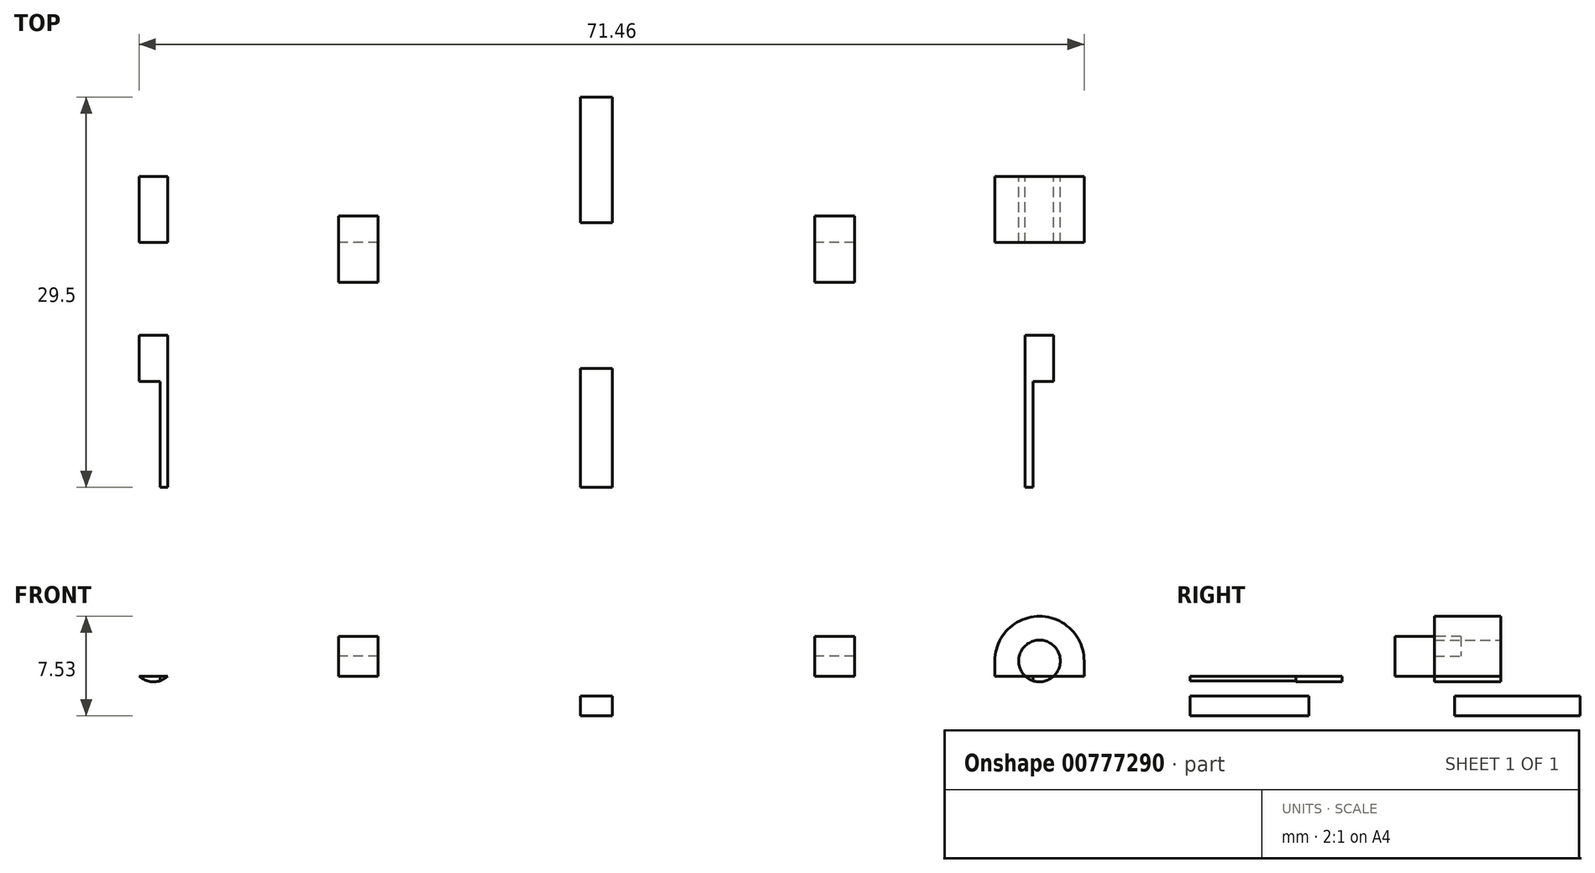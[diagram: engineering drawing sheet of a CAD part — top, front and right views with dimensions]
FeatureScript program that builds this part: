
annotation { "Feature Type Name" : "Feature", "Feature Type Description" : "" }
export const myFeature = defineFeature(function(context is Context, id is Id, definition is map)
    precondition{}
    {
        {
            var Q0;
            Q0=qCreatedBy(makeId("Top.planeOp"),FACE);
            var sketch = newSketch(context, id + "F0", { "sketchPlane" : qUnion([Q0])});
            skLineSegment(sketch, "E0.bottom", {"start": v(-40, 11.75) * mm, "end": v(40, 11.75) * mm});
            skLineSegment(sketch, "E0.top", {"start": v(-40, -11.75) * mm, "end": v(40, -11.75) * mm});
            skLineSegment(sketch, "E0.left", {"start": v(-40, 11.75) * mm, "end": v(-40, -11.75) * mm});
            skLineSegment(sketch, "E0.right", {"start": v(40, 11.75) * mm, "end": v(40, -11.75) * mm});
            skLineSegment(sketch, "E1", {"start": v(-83.31, 0) * mm, "end": v(90.72, 0) * mm, "construction": true});
            skLineSegment(sketch, "E2", {"start": v(0, 73.48) * mm, "end": v(0, -78.32) * mm, "construction": true});
            skLineSegment(sketch, "E3.bottom", {"start": v(-40, -11.75) * mm, "end": v(-33, -11.75) * mm});
            skLineSegment(sketch, "E3.top", {"start": v(-40, -3.75) * mm, "end": v(-33, -3.75) * mm});
            skLineSegment(sketch, "E3.left", {"start": v(-40, -11.75) * mm, "end": v(-40, -3.75) * mm});
            skLineSegment(sketch, "E3.right", {"start": v(-33, -11.75) * mm, "end": v(-33, -3.75) * mm});
            skLineSegment(sketch, "E4.bottom", {"start": v(40, -11.75) * mm, "end": v(33, -11.75) * mm});
            skLineSegment(sketch, "E4.top", {"start": v(40, -3.75) * mm, "end": v(33, -3.75) * mm});
            skLineSegment(sketch, "E4.left", {"start": v(40, -11.75) * mm, "end": v(40, -3.75) * mm});
            skLineSegment(sketch, "E4.right", {"start": v(33, -11.75) * mm, "end": v(33, -3.75) * mm});
            skLineSegment(sketch, "E5.bottom", {"start": v(-3, 8.25) * mm, "end": v(3, 8.25) * mm});
            skLineSegment(sketch, "E5.top", {"start": v(-3, -2.75) * mm, "end": v(3, -2.75) * mm});
            skLineSegment(sketch, "E5.left", {"start": v(-3, 8.25) * mm, "end": v(-3, -2.75) * mm});
            skLineSegment(sketch, "E5.right", {"start": v(3, 8.25) * mm, "end": v(3, -2.75) * mm});
            skLineSegment(sketch, "E6.bottom", {"start": v(-19.5, 8.75) * mm, "end": v(-16.5, 8.75) * mm});
            skLineSegment(sketch, "E6.top", {"start": v(-19.5, 3.75) * mm, "end": v(-16.5, 3.75) * mm});
            skLineSegment(sketch, "E6.left", {"start": v(-19.5, 8.75) * mm, "end": v(-19.5, 3.75) * mm});
            skLineSegment(sketch, "E6.right", {"start": v(-16.5, 8.75) * mm, "end": v(-16.5, 3.75) * mm});
            skLineSegment(sketch, "E7.bottom", {"start": v(16.5, 8.75) * mm, "end": v(19.5, 8.75) * mm});
            skLineSegment(sketch, "E7.top", {"start": v(16.5, 3.75) * mm, "end": v(19.5, 3.75) * mm});
            skLineSegment(sketch, "E7.left", {"start": v(16.5, 8.75) * mm, "end": v(16.5, 3.75) * mm});
            skLineSegment(sketch, "E7.right", {"start": v(19.5, 8.75) * mm, "end": v(19.5, 3.75) * mm});
            skLineSegment(sketch, "E8.bottom", {"start": v(37, -0.25) * mm, "end": v(30, -0.25) * mm});
            skLineSegment(sketch, "E8.top", {"start": v(37, 6.75) * mm, "end": v(30, 6.75) * mm});
            skLineSegment(sketch, "E8.left", {"start": v(37, -0.25) * mm, "end": v(37, 6.75) * mm});
            skLineSegment(sketch, "E8.right", {"start": v(30, -0.25) * mm, "end": v(30, 6.75) * mm});
            skLineSegment(sketch, "E9.MirrorCS", {"start": v(-30, -0.25) * mm, "end": v(-30, 6.75) * mm});
            skLineSegment(sketch, "E10.MirrorCS", {"start": v(-37, -0.25) * mm, "end": v(-37, 6.75) * mm});
            skLineSegment(sketch, "E11.MirrorCS", {"start": v(-37, -0.25) * mm, "end": v(-30, -0.25) * mm});
            skLineSegment(sketch, "E12.MirrorCS", {"start": v(-37, 6.75) * mm, "end": v(-30, 6.75) * mm});
            skSolve(sketch);
        }
        {
            var Q0;
            Q0=makeQuery(id+"F0.imprint","IMPRINT",FACE,{"disambiguationData":[TD([[makeQuery(id+"F0.imprint","IMPRINT",EDGE,{"derivedFrom":sQuery(id+"F0.wireOp",EDGE,"E0.bottom")}),-1.0]])]});
            extrude(context, id + "F1", {"entities" : qUnion([Q0]), "depth" : 3 * mm, "offsetDistance" : 25 * mm});
        }
        {
            var Q0;
            Q0=makeQuery(id+"F0.imprint","IMPRINT",FACE,{"disambiguationData":[TD([[makeQuery(id+"F0.imprint","IMPRINT",EDGE,{"derivedFrom":sQuery(id+"F0.wireOp",EDGE,"E6.bottom")}),-1.0]])]});
            var Q1;
            Q1=makeQuery(id+"F0.imprint","IMPRINT",FACE,{"disambiguationData":[TD([[makeQuery(id+"F0.imprint","IMPRINT",EDGE,{"derivedFrom":sQuery(id+"F0.wireOp",EDGE,"E7.bottom")}),-1.0]])]});
            extrude(context, id + "F2", {"entities" : qUnion([Q0, Q1]), "operationType" : NewBodyOperationType.ADD, "depth" : 6 * mm, "offsetDistance" : 25 * mm});
        }
        {
            var Q0;
            Q0=makeQuery(id+"F2.opExtrude","SWEPT_FACE",FACE,{"disambiguationData":[OSD([sQuery(id+"F0.wireOp",EDGE,"E7.bottom")])]});
            var sketch = newSketch(context, id + "F3", { "sketchPlane" : qUnion([Q0])});
            skLineSegment(sketch, "E13", {"start": v(-19.5, 4.5) * mm, "end": v(-16.5, 4.5) * mm});
            skSolve(sketch);
        }
        {
            var Q0;
            {var subQ0=sQuery(id+"F3.wireOp",EDGE,"E13");Q0=makeQuery(id+"F3.imprint","IMPRINT",FACE,{"disambiguationData":[TD([[makeQuery(id+"F3.imprint","IMPRINT",EDGE,{"derivedFrom":subQ0}),-1.0]])]});}
            extrude(context, id + "F4", {"entities" : qUnion([Q0]), "operationType" : NewBodyOperationType.REMOVE, "oppositeDirection" : true, "depth" : 2 * mm, "offsetDistance" : 25 * mm});
        }
        {
            var Q0;
            Q0=makeQuery(id+"F2.opExtrude","SWEPT_FACE",FACE,{"disambiguationData":[OSD([sQuery(id+"F0.wireOp",EDGE,"E6.bottom")])]});
            var sketch = newSketch(context, id + "F5", { "sketchPlane" : qUnion([Q0])});
            skLineSegment(sketch, "E14", {"start": v(16.5, 4.5) * mm, "end": v(19.5, 4.5) * mm});
            skSolve(sketch);
        }
        {
            var Q0;
            {var subQ0=sQuery(id+"F5.wireOp",EDGE,"E14");Q0=makeQuery(id+"F5.imprint","IMPRINT",FACE,{"disambiguationData":[TD([[makeQuery(id+"F5.imprint","IMPRINT",EDGE,{"derivedFrom":subQ0}),-1.0]])]});}
            extrude(context, id + "F6", {"entities" : qUnion([Q0]), "operationType" : NewBodyOperationType.REMOVE, "oppositeDirection" : true, "depth" : 2 * mm, "offsetDistance" : 25 * mm});
        }
        {
            var Q0;
            Q0=makeQuery(id+"F1.opExtrude","SWEPT_FACE",FACE,{"disambiguationData":[OSD([sQuery(id+"F0.wireOp",EDGE,"E0.bottom")])]});
            var sketch = newSketch(context, id + "F7", { "sketchPlane" : qUnion([Q0])});
            skLineSegment(sketch, "E15.bottom", {"start": v(-1.2, 0) * mm, "end": v(1.2, 0) * mm});
            skLineSegment(sketch, "E15.top", {"start": v(-1.2, 1.5) * mm, "end": v(1.2, 1.5) * mm});
            skLineSegment(sketch, "E15.left", {"start": v(-1.2, 0) * mm, "end": v(-1.2, 1.5) * mm});
            skLineSegment(sketch, "E15.right", {"start": v(1.2, 0) * mm, "end": v(1.2, 1.5) * mm});
            skLineSegment(sketch, "E16", {"start": v(0, 3) * mm, "end": v(0, 0) * mm, "construction": true});
            skSolve(sketch);
        }
        {
            var Q0;
            Q0=makeQuery(id+"F7.imprint","IMPRINT",FACE,{"disambiguationData":[TD([[makeQuery(id+"F7.imprint","IMPRINT",EDGE,{"derivedFrom":sQuery(id+"F7.wireOp",EDGE,"E15.bottom")}),-1.0]])]});
            extrude(context, id + "F8", {"entities" : qUnion([Q0]), "operationType" : NewBodyOperationType.ADD, "depth" : 6 * mm, "offsetDistance" : 25 * mm});
        }
        {
            var Q0;
            Q0=makeQuery(id+"F1.opExtrude","SWEPT_FACE",FACE,{"disambiguationData":[OSD([sQuery(id+"F0.wireOp",EDGE,"E0.top")])]});
            var sketch = newSketch(context, id + "F9", { "sketchPlane" : qUnion([Q0])});
            skLineSegment(sketch, "E17", {"start": v(-27, 3) * mm, "end": v(-27, 0) * mm, "construction": true});
            skLineSegment(sketch, "E18", {"start": v(-19, 3) * mm, "end": v(-19, 0) * mm, "construction": true});
            skLineSegment(sketch, "E19", {"start": v(19, 3) * mm, "end": v(19, 0) * mm, "construction": true});
            skLineSegment(sketch, "E20", {"start": v(27, 3) * mm, "end": v(27, 0) * mm, "construction": true});
            skLineSegment(sketch, "E21", {"start": v(-33, 3) * mm, "end": v(33, 3) * mm, "construction": true});
            skCircle(sketch, "E22", {"center": v(-27, 3) * mm, "radius": 3 * mm});
            skCircle(sketch, "E23", {"center": v(-19, 3) * mm, "radius": 3 * mm});
            skCircle(sketch, "E24", {"center": v(19, 3) * mm, "radius": 3 * mm});
            skCircle(sketch, "E25", {"center": v(27, 3) * mm, "radius": 3 * mm});
            skSolve(sketch);
        }
        {
            var Q0;
            {var subQ0=sQuery(id+"F9.wireOp",EDGE,"E22");var subQ1=makeQuery(id+"F1.opExtrude","CAP_EDGE",EDGE,{"disambiguationData":[OSD([sQuery(id+"F0.wireOp",EDGE,"E0.top")])],"isStart":false});var subQ2=makeQuery(id+"F9.imprint","INTERSECT",VERTEX,{"disambiguationData":[OD(0.0)],"derivedFrom":[subQ1,subQ0]});Q0=makeQuery(id+"F9.imprint","IMPRINT",FACE,{"disambiguationData":[TD([[makeQuery(id+"F9.imprint","IMPRINT",EDGE,{"disambiguationData":[TD([[subQ2,1.0]])],"derivedFrom":subQ0}),1.0]])]});}
            var Q1;
            {var subQ0=sQuery(id+"F9.wireOp",EDGE,"E23");var subQ1=makeQuery(id+"F1.opExtrude","CAP_EDGE",EDGE,{"disambiguationData":[OSD([sQuery(id+"F0.wireOp",EDGE,"E0.top")])],"isStart":false});var subQ2=makeQuery(id+"F9.imprint","INTERSECT",VERTEX,{"disambiguationData":[OD(0.0)],"derivedFrom":[subQ1,subQ0]});Q1=makeQuery(id+"F9.imprint","IMPRINT",FACE,{"disambiguationData":[TD([[makeQuery(id+"F9.imprint","IMPRINT",EDGE,{"disambiguationData":[TD([[subQ2,1.0]])],"derivedFrom":subQ0}),1.0]])]});}
            var Q2;
            {var subQ0=sQuery(id+"F9.wireOp",EDGE,"E24");var subQ1=makeQuery(id+"F1.opExtrude","CAP_EDGE",EDGE,{"disambiguationData":[OSD([sQuery(id+"F0.wireOp",EDGE,"E0.top")])],"isStart":false});var subQ2=makeQuery(id+"F9.imprint","INTERSECT",VERTEX,{"disambiguationData":[OD(0.0)],"derivedFrom":[subQ1,subQ0]});Q2=makeQuery(id+"F9.imprint","IMPRINT",FACE,{"disambiguationData":[TD([[makeQuery(id+"F9.imprint","IMPRINT",EDGE,{"disambiguationData":[TD([[subQ2,1.0]])],"derivedFrom":subQ0}),1.0]])]});}
            var Q3;
            {var subQ0=sQuery(id+"F9.wireOp",EDGE,"E25");var subQ1=makeQuery(id+"F1.opExtrude","CAP_EDGE",EDGE,{"disambiguationData":[OSD([sQuery(id+"F0.wireOp",EDGE,"E0.top")])],"isStart":false});var subQ2=makeQuery(id+"F9.imprint","INTERSECT",VERTEX,{"disambiguationData":[OD(0.0)],"derivedFrom":[subQ1,subQ0]});Q3=makeQuery(id+"F9.imprint","IMPRINT",FACE,{"disambiguationData":[TD([[makeQuery(id+"F9.imprint","IMPRINT",EDGE,{"disambiguationData":[TD([[subQ2,1.0]])],"derivedFrom":subQ0}),1.0]])]});}
            extrude(context, id + "F10", {"entities" : qUnion([Q0, Q1, Q2, Q3]), "operationType" : NewBodyOperationType.ADD, "oppositeDirection" : true, "depth" : 7 * mm, "offsetDistance" : 25 * mm});
        }
        {
            var Q0;
            {var subQ0=sQuery(id+"F0.wireOp",EDGE,"E0.top");Q0=makeQuery(id+"F10.boolean.opBoolean","MERGE",FACE,{"derivedFrom":[makeQuery(id+"F1.opExtrude","SWEPT_FACE",FACE,{"disambiguationData":[OSD([subQ0])]}),makeQuery(id+"F10.opExtrude","CAP_FACE",FACE,{"disambiguationData":[OSD([subQ0,sQuery(id+"F9.wireOp",EDGE,"E22")])],"isStart":true}),makeQuery(id+"F10.opExtrude","CAP_FACE",FACE,{"disambiguationData":[OSD([subQ0,sQuery(id+"F9.wireOp",EDGE,"E23")])],"isStart":true}),makeQuery(id+"F10.opExtrude","CAP_FACE",FACE,{"disambiguationData":[OSD([subQ0,sQuery(id+"F9.wireOp",EDGE,"E24")])],"isStart":true}),makeQuery(id+"F10.opExtrude","CAP_FACE",FACE,{"disambiguationData":[OSD([subQ0,sQuery(id+"F9.wireOp",EDGE,"E25")])],"isStart":true})]});}
            var sketch = newSketch(context, id + "F11", { "sketchPlane" : qUnion([Q0])});
            skCircle(sketch, "E26", {"center": v(-27, 3) * mm, "radius": 1.44 * mm});
            skCircle(sketch, "E27", {"center": v(-19, 3) * mm, "radius": 1.44 * mm});
            skCircle(sketch, "E28", {"center": v(19, 3) * mm, "radius": 1.44 * mm});
            skCircle(sketch, "E29", {"center": v(27, 3) * mm, "radius": 1.44 * mm});
            skSolve(sketch);
        }
        {
            var Q0;
            Q0=makeQuery(id+"F11.imprint","IMPRINT",FACE,{"disambiguationData":[TD([[makeQuery(id+"F11.imprint","IMPRINT",EDGE,{"derivedFrom":sQuery(id+"F11.wireOp",EDGE,"E26")}),1.0]])]});
            var Q1;
            Q1=makeQuery(id+"F11.imprint","IMPRINT",FACE,{"disambiguationData":[TD([[makeQuery(id+"F11.imprint","IMPRINT",EDGE,{"derivedFrom":sQuery(id+"F11.wireOp",EDGE,"E27")}),1.0]])]});
            var Q2;
            Q2=makeQuery(id+"F11.imprint","IMPRINT",FACE,{"disambiguationData":[TD([[makeQuery(id+"F11.imprint","IMPRINT",EDGE,{"derivedFrom":sQuery(id+"F11.wireOp",EDGE,"E28")}),1.0]])]});
            var Q3;
            Q3=makeQuery(id+"F11.imprint","IMPRINT",FACE,{"disambiguationData":[TD([[makeQuery(id+"F11.imprint","IMPRINT",EDGE,{"derivedFrom":sQuery(id+"F11.wireOp",EDGE,"E29")}),1.0]])]});
            extrude(context, id + "F12", {"entities" : qUnion([Q0, Q1, Q2, Q3]), "operationType" : NewBodyOperationType.REMOVE, "oppositeDirection" : true, "depth" : 4 * mm, "offsetDistance" : 25 * mm});
        }
        {
            var Q0;
            Q0=makeQuery(id+"F1.opExtrude","SWEPT_FACE",FACE,{"disambiguationData":[OSD([sQuery(id+"F0.wireOp",EDGE,"E0.bottom")])]});
            var sketch = newSketch(context, id + "F13", { "sketchPlane" : qUnion([Q0])});
            skArc(sketch, "E30", {"start": v(-30.13, 4.15) * mm, "mid": v(-33.5, 7.52) * mm, "end": v(-36.87, 4.13) * mm});
            skCircle(sketch, "E31", {"center": v(-33.5, 4.15) * mm, "radius": 1.57 * mm});
            skLineSegment(sketch, "E32", {"start": v(-36.87, 4.13) * mm, "end": v(-36.87, 3) * mm});
            skLineSegment(sketch, "E33", {"start": v(-30.13, 4.15) * mm, "end": v(-30.13, 3) * mm});
            skLineSegment(sketch, "E34", {"start": v(0, 0) * mm, "end": v(0, 3) * mm, "construction": true});
            skLineSegment(sketch, "E35.MirrorCS", {"start": v(30.13, 4.15) * mm, "end": v(30.13, 3) * mm});
            skLineSegment(sketch, "E36.MirrorCS", {"start": v(36.87, 4.13) * mm, "end": v(36.87, 3) * mm});
            skCircle(sketch, "E37.MirrorC", {"center": v(33.5, 4.15) * mm, "radius": 1.57 * mm});
            skArc(sketch, "E38.MirrorCS", {"start": v(30.13, 4.15) * mm, "mid": v(33.5, 7.52) * mm, "end": v(36.87, 4.13) * mm});
            skSolve(sketch);
        }
        {
            var Q0;
            Q0=makeQuery(id+"F13.imprint","IMPRINT",FACE,{"disambiguationData":[TD([[makeQuery(id+"F13.imprint","IMPRINT",EDGE,{"derivedFrom":sQuery(id+"F13.wireOp",EDGE,"E30")}),1.0]])]});
            var Q1;
            {var subQ0=sQuery(id+"F13.wireOp",EDGE,"E31");var subQ1=makeQuery(id+"F1.opExtrude","CAP_EDGE",EDGE,{"disambiguationData":[OSD([sQuery(id+"F0.wireOp",EDGE,"E0.bottom")])],"isStart":false});var subQ2=makeQuery(id+"F13.imprint","INTERSECT",VERTEX,{"disambiguationData":[OD(0.0)],"derivedFrom":[subQ1,subQ0]});Q1=makeQuery(id+"F13.imprint","IMPRINT",FACE,{"disambiguationData":[TD([[makeQuery(id+"F13.imprint","IMPRINT",EDGE,{"disambiguationData":[TD([[subQ2,1.0]])],"derivedFrom":subQ0}),1.0]])]});}
            extrude(context, id + "F14", {"entities" : qUnion([Q0, Q1]), "operationType" : NewBodyOperationType.ADD, "oppositeDirection" : true, "depth" : 5 * mm, "offsetDistance" : 25 * mm});
        }
        {
            var Q0;
            {var subQ0=sQuery(id+"F13.wireOp",EDGE,"E31");var subQ1=makeQuery(id+"F1.opExtrude","CAP_EDGE",EDGE,{"disambiguationData":[OSD([sQuery(id+"F0.wireOp",EDGE,"E0.bottom")])],"isStart":false});var subQ2=makeQuery(id+"F13.imprint","INTERSECT",VERTEX,{"disambiguationData":[OD(0.0)],"derivedFrom":[subQ1,subQ0]});Q0=makeQuery(id+"F13.imprint","IMPRINT",FACE,{"disambiguationData":[TD([[makeQuery(id+"F13.imprint","IMPRINT",EDGE,{"disambiguationData":[TD([[subQ2,1.0]])],"derivedFrom":subQ0}),1.0]])]});}
            var Q1;
            {var subQ0=sQuery(id+"F13.wireOp",EDGE,"E31");var subQ1=makeQuery(id+"F1.opExtrude","CAP_EDGE",EDGE,{"disambiguationData":[OSD([sQuery(id+"F0.wireOp",EDGE,"E0.bottom")])],"isStart":false});var subQ2=makeQuery(id+"F13.imprint","INTERSECT",VERTEX,{"disambiguationData":[OD(0.0)],"derivedFrom":[subQ1,subQ0]});Q1=makeQuery(id+"F13.imprint","IMPRINT",FACE,{"disambiguationData":[TD([[makeQuery(id+"F13.imprint","IMPRINT",EDGE,{"disambiguationData":[TD([[subQ2,-1.0]])],"derivedFrom":subQ0}),1.0]])]});}
            extrude(context, id + "F15", {"entities" : qUnion([Q0, Q1]), "operationType" : NewBodyOperationType.REMOVE, "endBound" : BoundingType.UP_TO_NEXT, "oppositeDirection" : true, "depth" : 25 * mm, "offsetDistance" : 25 * mm});
        }
        {
            var Q0;
            {var subQ5=sQuery(id+"F13.wireOp",EDGE,"E35.MirrorCS");Q0=makeQuery(id+"F13.imprint","IMPRINT",FACE,{"disambiguationData":[TD([[makeQuery(id+"F13.imprint","IMPRINT",EDGE,{"derivedFrom":subQ5}),1.0]])]});}
            var Q1;
            {var subQ0=sQuery(id+"F13.wireOp",EDGE,"E37.MirrorC");var subQ1=makeQuery(id+"F1.opExtrude","CAP_EDGE",EDGE,{"disambiguationData":[OSD([sQuery(id+"F0.wireOp",EDGE,"E0.bottom")])],"isStart":false});var subQ2=makeQuery(id+"F13.imprint","INTERSECT",VERTEX,{"disambiguationData":[OD(0.0)],"derivedFrom":[subQ1,subQ0]});Q1=makeQuery(id+"F13.imprint","IMPRINT",FACE,{"disambiguationData":[TD([[makeQuery(id+"F13.imprint","IMPRINT",EDGE,{"disambiguationData":[TD([[subQ2,1.0]])],"derivedFrom":subQ0}),-1.0]])]});}
            var Q2;
            {var subQ0=sQuery(id+"F13.wireOp",EDGE,"E37.MirrorC");var subQ1=makeQuery(id+"F1.opExtrude","CAP_EDGE",EDGE,{"disambiguationData":[OSD([sQuery(id+"F0.wireOp",EDGE,"E0.bottom")])],"isStart":false});var subQ2=makeQuery(id+"F13.imprint","INTERSECT",VERTEX,{"disambiguationData":[OD(0.0)],"derivedFrom":[subQ1,subQ0]});Q2=makeQuery(id+"F13.imprint","IMPRINT",FACE,{"disambiguationData":[TD([[makeQuery(id+"F13.imprint","IMPRINT",EDGE,{"disambiguationData":[TD([[subQ2,-1.0]])],"derivedFrom":subQ0}),-1.0]])]});}
            extrude(context, id + "F16", {"entities" : qUnion([Q0, Q1, Q2]), "operationType" : NewBodyOperationType.ADD, "oppositeDirection" : true, "depth" : 5 * mm, "offsetDistance" : 25 * mm});
        }
        {
            var Q0;
            {var subQ0=sQuery(id+"F13.wireOp",EDGE,"E37.MirrorC");var subQ1=makeQuery(id+"F1.opExtrude","CAP_EDGE",EDGE,{"disambiguationData":[OSD([sQuery(id+"F0.wireOp",EDGE,"E0.bottom")])],"isStart":false});var subQ2=makeQuery(id+"F13.imprint","INTERSECT",VERTEX,{"disambiguationData":[OD(0.0)],"derivedFrom":[subQ1,subQ0]});Q0=makeQuery(id+"F13.imprint","IMPRINT",FACE,{"disambiguationData":[TD([[makeQuery(id+"F13.imprint","IMPRINT",EDGE,{"disambiguationData":[TD([[subQ2,-1.0]])],"derivedFrom":subQ0}),-1.0]])]});}
            var Q1;
            {var subQ0=sQuery(id+"F13.wireOp",EDGE,"E37.MirrorC");var subQ1=makeQuery(id+"F1.opExtrude","CAP_EDGE",EDGE,{"disambiguationData":[OSD([sQuery(id+"F0.wireOp",EDGE,"E0.bottom")])],"isStart":false});var subQ2=makeQuery(id+"F13.imprint","INTERSECT",VERTEX,{"disambiguationData":[OD(0.0)],"derivedFrom":[subQ1,subQ0]});Q1=makeQuery(id+"F13.imprint","IMPRINT",FACE,{"disambiguationData":[TD([[makeQuery(id+"F13.imprint","IMPRINT",EDGE,{"disambiguationData":[TD([[subQ2,1.0]])],"derivedFrom":subQ0}),-1.0]])]});}
            extrude(context, id + "F17", {"entities" : qUnion([Q0, Q1]), "operationType" : NewBodyOperationType.REMOVE, "endBound" : BoundingType.UP_TO_NEXT, "oppositeDirection" : true, "depth" : 25 * mm, "offsetDistance" : 25 * mm});
        }
    });
